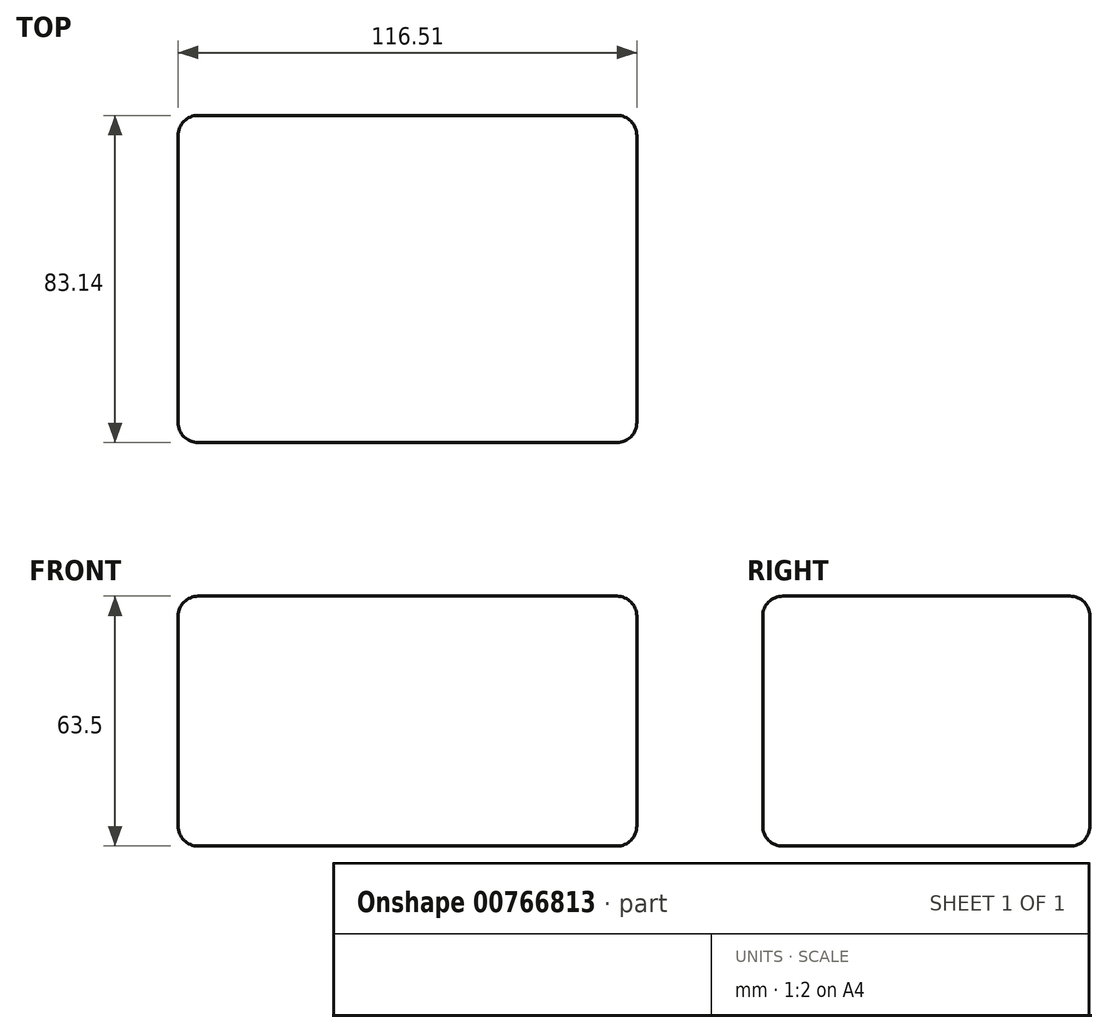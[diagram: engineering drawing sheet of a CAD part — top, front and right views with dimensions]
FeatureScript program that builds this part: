
annotation { "Feature Type Name" : "Feature", "Feature Type Description" : "" }
export const myFeature = defineFeature(function(context is Context, id is Id, definition is map)
    precondition{}
    {
        {
            var Q0;
            Q0=qCreatedBy(makeId("Top.planeOp"),FACE);
            var sketch = newSketch(context, id + "F0", { "sketchPlane" : qUnion([Q0])});
            skLineSegment(sketch, "E0.bottom", {"start": v(-58.13, 43.95) * mm, "end": v(58.38, 43.95) * mm});
            skLineSegment(sketch, "E0.top", {"start": v(-58.13, -39.19) * mm, "end": v(58.38, -39.19) * mm});
            skLineSegment(sketch, "E0.left", {"start": v(-58.13, 43.95) * mm, "end": v(-58.13, -39.19) * mm});
            skLineSegment(sketch, "E0.right", {"start": v(58.38, 43.95) * mm, "end": v(58.38, -39.19) * mm});
            skSolve(sketch);
        }
        {
            var Q0;
            Q0=makeQuery(id+"F0.imprint","IMPRINT",FACE,{"disambiguationData":[TD([[makeQuery(id+"F0.imprint","IMPRINT",EDGE,{"derivedFrom":sQuery(id+"F0.wireOp",EDGE,"E0.bottom")}),-1.0]])]});
            extrude(context, id + "F1", {"entities" : qUnion([Q0]), "oppositeDirection" : true, "depth" : 63.5 * mm, "offsetDistance" : 25.4 * mm});
        }
        {
            var Q0;
            Q0=makeQuery(id+"F1.opExtrude","SWEPT_FACE",FACE,{"disambiguationData":[OSD([sQuery(id+"F0.wireOp",EDGE,"E0.left")])]});
            var Q1;
            Q1=makeQuery(id+"F1.opExtrude","SWEPT_FACE",FACE,{"disambiguationData":[OSD([sQuery(id+"F0.wireOp",EDGE,"E0.top")])]});
            var Q2;
            Q2=makeQuery(id+"F1.opExtrude","CAP_FACE",FACE,{"disambiguationData":[OSD([sQuery(id+"F0.wireOp",EDGE,"E0.bottom"),sQuery(id+"F0.wireOp",EDGE,"E0.top"),sQuery(id+"F0.wireOp",EDGE,"E0.left"),sQuery(id+"F0.wireOp",EDGE,"E0.right")])],"isStart":true});
            var Q3;
            Q3=makeQuery(id+"F1.opExtrude","SWEPT_FACE",FACE,{"disambiguationData":[OSD([sQuery(id+"F0.wireOp",EDGE,"E0.right")])]});
            var Q4;
            Q4=makeQuery(id+"F1.opExtrude","SWEPT_FACE",FACE,{"disambiguationData":[OSD([sQuery(id+"F0.wireOp",EDGE,"E0.bottom")])]});
            var Q5;
            Q5=makeQuery(id+"F1.opExtrude","CAP_FACE",FACE,{"disambiguationData":[OSD([sQuery(id+"F0.wireOp",EDGE,"E0.bottom"),sQuery(id+"F0.wireOp",EDGE,"E0.top"),sQuery(id+"F0.wireOp",EDGE,"E0.left"),sQuery(id+"F0.wireOp",EDGE,"E0.right")])],"isStart":false});
            fillet(context, id + "F2", {"entities" : qUnion([Q0, Q1, Q2, Q3, Q4, Q5]), "radius" : 5.08 * mm, "tangentPropagation" : true, "allowEdgeOverflow" : false});
        }
    });
